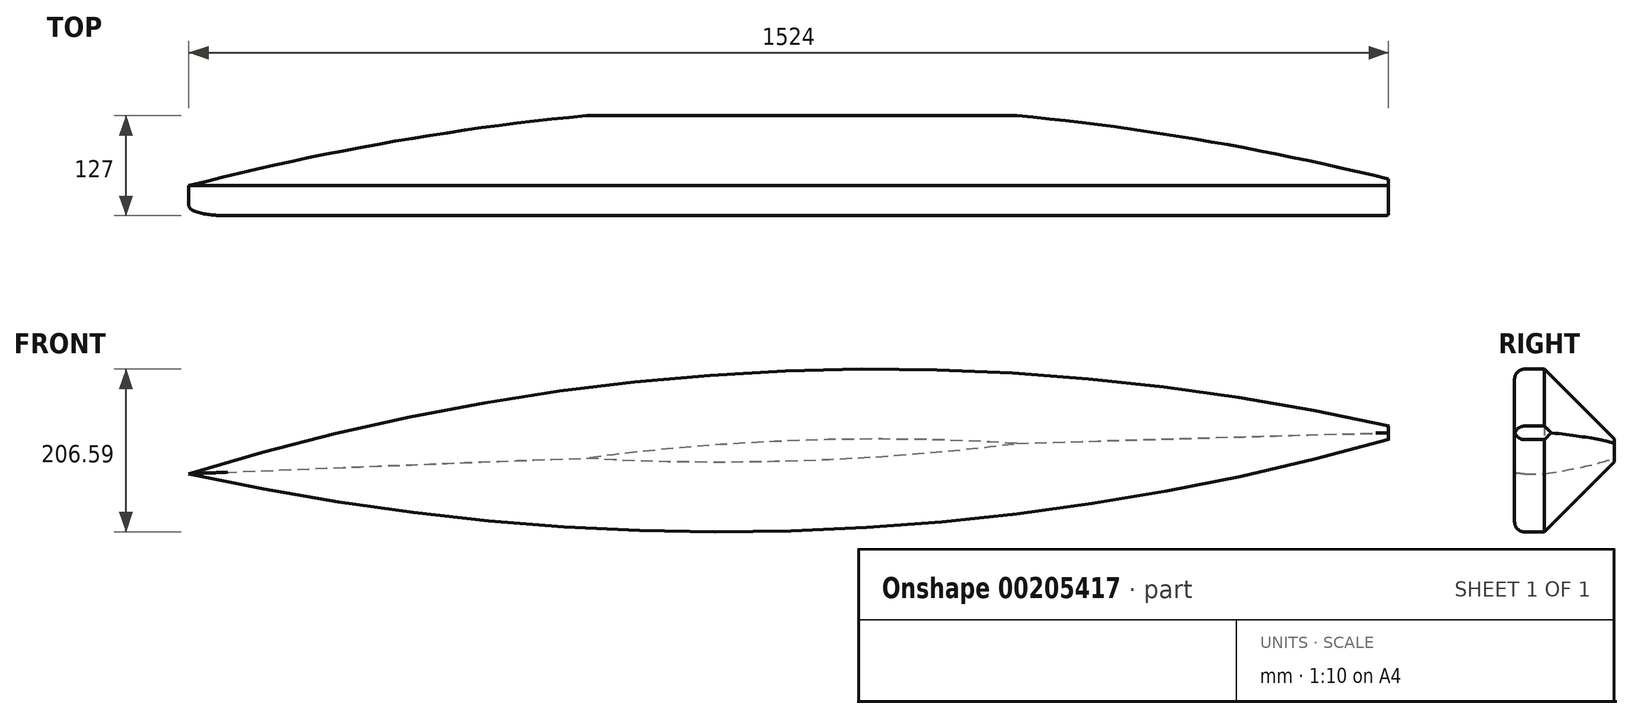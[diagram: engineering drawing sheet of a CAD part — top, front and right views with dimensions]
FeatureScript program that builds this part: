
annotation { "Feature Type Name" : "Feature", "Feature Type Description" : "" }
export const myFeature = defineFeature(function(context is Context, id is Id, definition is map)
    precondition{}
    {
        {
            var Q0;
            Q0=qCreatedBy(makeId("Front.planeOp"),FACE);
            var sketch = newSketch(context, id + "F0", { "sketchPlane" : qUnion([Q0])});
            skArc(sketch, "E0", {"start": v(1083.59, 60.58) * mm, "mid": v(317.6, 130.6) * mm, "end": v(-440.41, 0) * mm});
            skArc(sketch, "E1", {"start": v(-440.41, 0) * mm, "mid": v(324.27, -72.4) * mm, "end": v(1083.59, 43.44) * mm});
            skLineSegment(sketch, "E2", {"start": v(1083.59, 60.58) * mm, "end": v(1083.59, 43.44) * mm});
            skSolve(sketch);
        }
        {
            var Q0;
            Q0=makeQuery(id+"F0.imprint","IMPRINT",FACE,{"disambiguationData":[TD([[makeQuery(id+"F0.imprint","IMPRINT",EDGE,{"derivedFrom":sQuery(id+"F0.wireOp",EDGE,"E0")}),1.0]])]});
            extrude(context, id + "F1", {"entities" : qUnion([Q0]), "depth" : 127 * mm});
        }
        {
            var Q0;
            Q0=makeQuery(id+"F1.opExtrude","CAP_FACE",FACE,{"disambiguationData":[OSD([sQuery(id+"F0.wireOp",EDGE,"E0"),sQuery(id+"F0.wireOp",EDGE,"E1"),sQuery(id+"F0.wireOp",EDGE,"E2")])],"isStart":false});
            fillet(context, id + "F2", {"entities" : qUnion([Q0]), "radius" : 12.26 * mm, "tangentPropagation" : true, "allowEdgeOverflow" : false});
        }
        {
            var Q0;
            Q0=makeQuery(id+"F1.opExtrude","CAP_EDGE",EDGE,{"disambiguationData":[OSD([sQuery(id+"F0.wireOp",EDGE,"E1")])],"isStart":true});
            var Q1;
            Q1=makeQuery(id+"F1.opExtrude","CAP_EDGE",EDGE,{"disambiguationData":[OSD([sQuery(id+"F0.wireOp",EDGE,"E0")])],"isStart":true});
            chamfer(context, id + "F3", {"entities" : qUnion([Q0, Q1]), "width" : 88.9 * mm});
        }
    });
